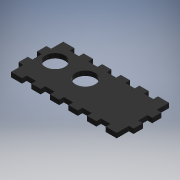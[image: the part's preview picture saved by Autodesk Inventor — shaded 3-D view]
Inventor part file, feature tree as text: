
AUTODESK INVENTOR PART (.ipt)
format: ipt  version: 2019 (Build 230136000, 136)  size: 202,240 bytes
history: native  units: mm
features: extrude x2, sketch x2
ambient origin geometry x8: Origin, YZ Plane, XZ Plane, XY Plane, X Axis, Y Axis, Z Axis, Center Point
bodies: Solid1 (feature_tree)
feature tree (4):
  extrude  "Extrusion1"  Depth=45.0mm
  extrude  "Extrusion2"  Depth=4.0mm
  sketch  "Sketch1"  dims[d0=99.0mm d1=45.0mm]
  sketch  "Sketch2"  dims[d2=17.0mm d3=15.0mm d4=27.0mm d5=26.0mm d6=4.0mm d7=0.0mm d8=4.0mm d11=8.0mm d12=4.0mm d14=8.0mm d15=8.0mm d16=8.0mm d17=4.0mm d18=8.0mm d19=4.0mm d20=0.0mm]
